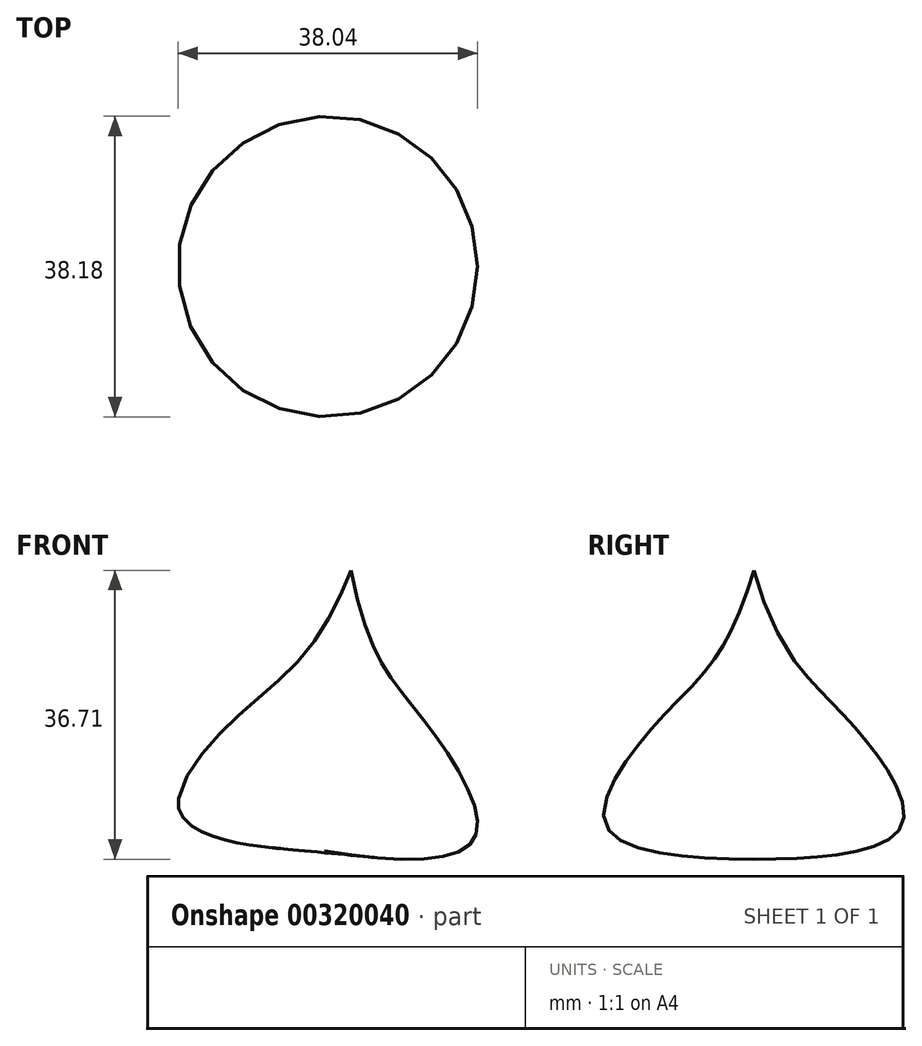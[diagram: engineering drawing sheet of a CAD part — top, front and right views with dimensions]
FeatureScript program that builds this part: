
annotation { "Feature Type Name" : "Feature", "Feature Type Description" : "" }
export const myFeature = defineFeature(function(context is Context, id is Id, definition is map)
    precondition{}
    {
        {
            var Q0;
            Q0=qCreatedBy(makeId("Front.planeOp"),FACE);
            var sketch = newSketch(context, id + "F0", { "sketchPlane" : qUnion([Q0])});
            skFitSpline(sketch, "E0", {"points": [v(-9.58, 25.8) * mm, v(0, 6.35) * mm, v(6.2, -8.08) * mm, v(-12.95, -9.8) * mm], "startDerivative": vector(18.16, -95.68) * mm, "endDerivative": vector(-79.46, 13.36) * mm});
            skLineSegment(sketch, "E1", {"start": v(-12.95, -9.8) * mm, "end": v(-9.58, 25.8) * mm});
            skSolve(sketch);
        }
        {
            var Q0;
            Q0=makeQuery(id+"F0.imprint","IMPRINT",FACE,{"disambiguationData":[TD([[makeQuery(id+"F0.imprint","IMPRINT",EDGE,{"derivedFrom":sQuery(id+"F0.wireOp",EDGE,"E0")}),-1.0]])]});
            var Q1;
            Q1=sQuery(id+"F0.wireOp",EDGE,"E1");
            revolve(context, id + "F1", {"entities" : qUnion([Q0]), "axis" : qUnion([Q1]), "revolveType" : RevolveType.FULL});
        }
    });
